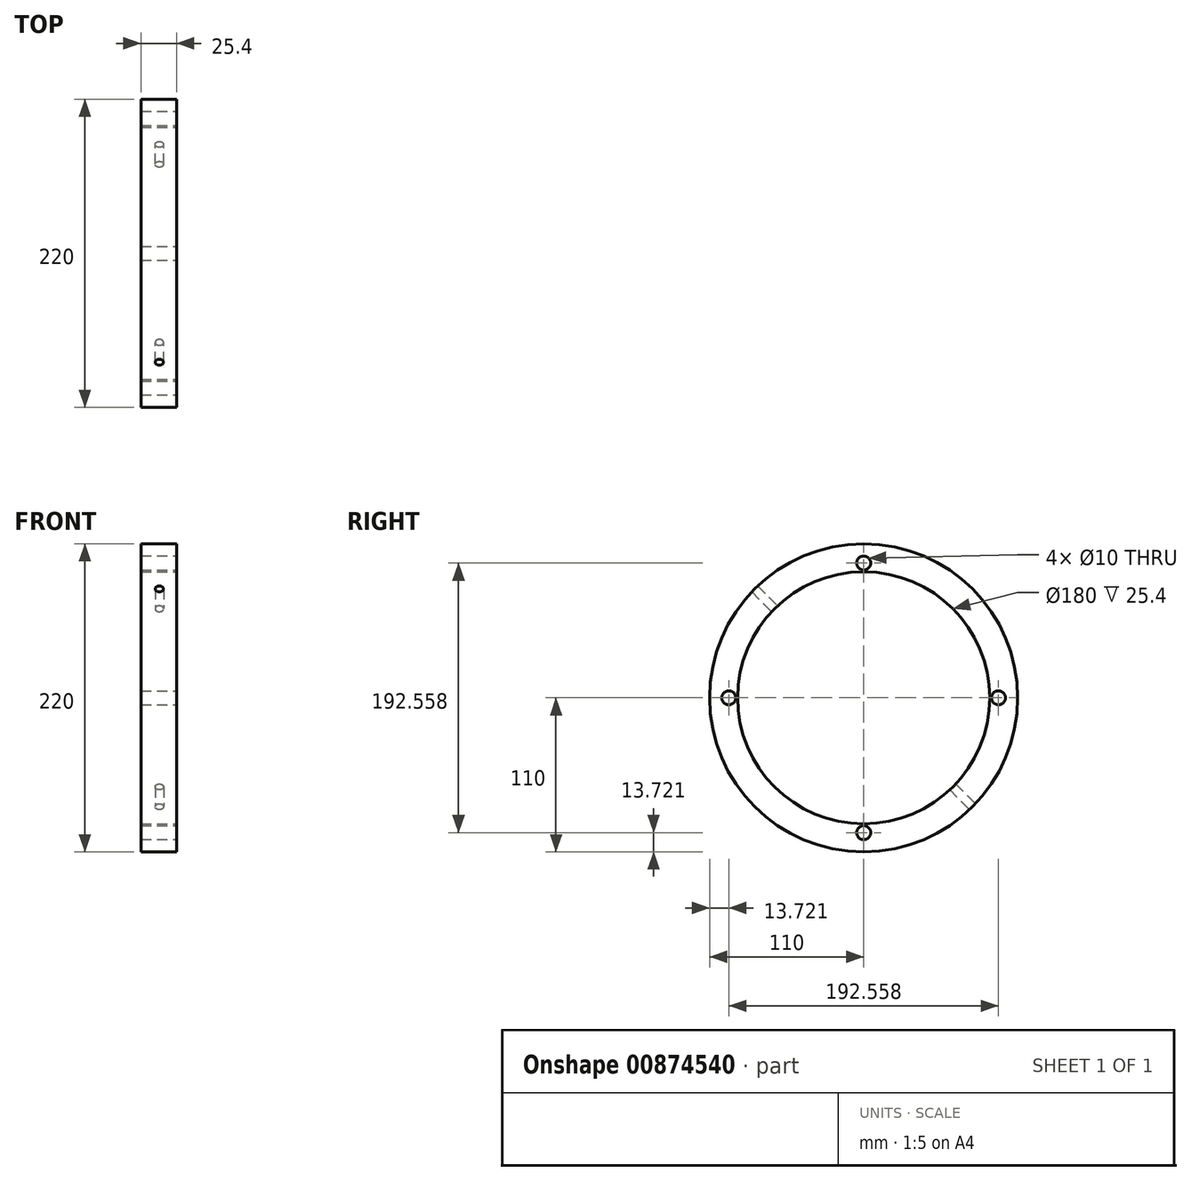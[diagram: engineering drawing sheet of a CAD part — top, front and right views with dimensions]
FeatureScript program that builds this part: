
annotation { "Feature Type Name" : "Feature", "Feature Type Description" : "" }
export const myFeature = defineFeature(function(context is Context, id is Id, definition is map)
    precondition{}
    {
        {
            var Q0;
            Q0=qCreatedBy(makeId("Right.planeOp"),FACE);
            var sketch = newSketch(context, id + "F0", { "sketchPlane" : qUnion([Q0])});
            skCircle(sketch, "E0", {"center": v(0, 0) * mm, "radius": 110 * mm});
            skCircle(sketch, "E1", {"center": v(0, 0) * mm, "radius": 90 * mm});
            skSolve(sketch);
        }
        {
            var Q0;
            Q0=makeQuery(id+"F0.imprint","IMPRINT",FACE,{"disambiguationData":[TD([[makeQuery(id+"F0.imprint","IMPRINT",EDGE,{"derivedFrom":sQuery(id+"F0.wireOp",EDGE,"E0")}),1.0]])]});
            var Q1;
            Q1=sQuery(id+"F0.wireOp",EDGE,"E0");
            var Q2;
            Q2=sQuery(id+"F0.wireOp",EDGE,"E1");
            extrude(context, id + "F1", {"entities" : qUnion([Q0]), "surfaceEntities" : qUnion([Q1, Q2]), "oppositeDirection" : true, "depth" : 25.4 * mm, "offsetDistance" : 25 * mm});
        }
        {
            var Q0;
            Q0=qCreatedBy(makeId("Top.planeOp"),FACE);
            var sketch = newSketch(context, id + "F2", { "sketchPlane" : qUnion([Q0])});
            skLineSegment(sketch, "E2", {"start": v(-76.01, 0) * mm, "end": v(75.4, 0) * mm});
            skSolve(sketch);
        }
        {
            var Q0;
            Q0=sQuery(id+"F2.wireOp",EDGE,"E2");
            cPlane(context, id + "F3", {"entities" : qUnion([Q0]), "cplaneType" : CPlaneType.LINE_ANGLE, "offset" : 25 * mm, "angle" : 45 * degree, "oppositeDirection" : true, "width" : 150 * mm, "height" : 150 * mm});
        }
        {
            var Q0;
            Q0=qCreatedBy(id+"F3.planeOp",FACE);
            var sketch = newSketch(context, id + "F4", { "sketchPlane" : qUnion([Q0])});
            skCircle(sketch, "E3", {"center": v(12.22, 0) * mm, "radius": 3 * mm});
            skSolve(sketch);
        }
        {
            var Q0;
            Q0=makeQuery(id+"F4.imprint","IMPRINT",FACE,{"disambiguationData":[TD([[makeQuery(id+"F4.imprint","IMPRINT",EDGE,{"derivedFrom":sQuery(id+"F4.wireOp",EDGE,"E3")}),1.0]])]});
            extrude(context, id + "F5", {"entities" : qUnion([Q0]), "operationType" : NewBodyOperationType.REMOVE, "endBound" : BoundingType.SYMMETRIC, "oppositeDirection" : true, "depth" : 221 * mm, "offsetDistance" : 25 * mm});
        }
        {
            var Q0;
            Q0=makeQuery(id+"F1.opExtrude","CAP_FACE",FACE,{"disambiguationData":[OSD([sQuery(id+"F0.wireOp",EDGE,"E0"),sQuery(id+"F0.wireOp",EDGE,"E1")])],"isStart":true});
            var sketch = newSketch(context, id + "F6", { "sketchPlane" : qUnion([Q0])});
            skLineSegment(sketch, "E4", {"start": v(0, 0) * mm, "end": v(0, 96.2) * mm});
            skSolve(sketch);
        }
        {
            var Q0;
            Q0=makeQuery(id+"F6.imprint","IMPRINT",FACE,{"disambiguationData":[TD([[makeQuery(id+"F6.imprint","IMPRINT",EDGE,{"derivedFrom":makeQuery(id+"F1.opExtrude","CAP_EDGE",EDGE,{"disambiguationData":[OSD([sQuery(id+"F0.wireOp",EDGE,"E0")])],"isStart":true})}),1.0]])]});
            var sketch = newSketch(context, id + "F7", { "sketchPlane" : qUnion([Q0])});
            skCircle(sketch, "E5", {"center": v(0, 96.28) * mm, "radius": 5 * mm});
            skCircle(sketch, "E6.1.0", {"center": v(-96.28, 0) * mm, "radius": 5 * mm});
            skCircle(sketch, "E6.2.0", {"center": v(0, -96.28) * mm, "radius": 5 * mm});
            skCircle(sketch, "E6.3.0", {"center": v(96.28, 0) * mm, "radius": 5 * mm});
            skPoint(sketch, "E6.center", {"position": v(0, 0) * mm});
            skSolve(sketch);
        }
        {
            var Q0;
            Q0 = qSketchRegion(id + "F7", true);
            extrude(context, id + "F8", {"entities" : qUnion([Q0]), "operationType" : NewBodyOperationType.REMOVE, "oppositeDirection" : true, "depth" : 25.5 * mm, "offsetDistance" : 25 * mm});
        }
    });
